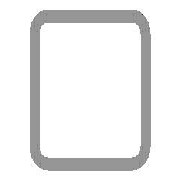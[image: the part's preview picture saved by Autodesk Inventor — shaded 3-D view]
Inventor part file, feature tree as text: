
AUTODESK INVENTOR PART (.ipt)
format: ipt  version: 2022 (Build 260153000, 153)  size: 545,792 bytes
history: native  units: mm (DEFAULTED — no unit token found)
features: other x11, surface_op x4, sketch x2, sweep x1, plane x1
ambient origin geometry x8: Origin, YZ Plane, XZ Plane, XY Plane, X Axis, Y Axis, Z Axis, Center Point
bodies: Solid1 (feature_tree), Body (feature_tree), Solid5 (feature_tree), Solid6 (feature_tree)
feature tree (19):
  parser-record x1  (decoder bookkeeping rows leaked as tree rows — omitted from the tree; the rows remain in map.json)
  other  "Driven Length"
  other  "Start Plane"
  other  "End Plane"
  sweep  "Sweep Path"
  other  "Orientation Work Plane"
  sketch  "Sketch3"  dims[d7=8.0mm d9=40.0mm]
  plane  "Work Plane3"
  sketch  "Sketch4"  dims[d11=40.0mm d12=4.0mm d13=-0.0mm d14=2479.411255mm d15=20.0mm d16=20.0mm d17=90.0deg d18=2479.411255mm d19=0.0mm d20=0.0mm d75=5.0mm d76=5.0mm d77=5.0mm d78=5.0mm d79=5.0mm d80=5.0mm d81=5.0mm d82=5.0mm d83=0.0mm d84=5.0mm d85=5.0mm d86=5.0mm d87=5.0mm d88=5.0mm d89=5.0mm d90=5.0mm d91=5.0mm d92=0.0mm d93=5.0mm d94=5.0mm d95=5.0mm d96=5.0mm d97=5.0mm d98=5.0mm d99=5.0mm d100=5.0mm d101=0.0mm d102=5.0mm d103=5.0mm d104=5.0mm d105=5.0mm d106=5.0mm d107=5.0mm d108=5.0mm d109=5.0mm d110=0.0mm]
  other  "Srf11"
  other  "Srf12"
  other  "Srf14"
  other  "Srf15"
  other  "Srf10"
  surface_op  "Boundary Patch7"
  surface_op  "Boundary Patch8"
  other  "Srf13"
  surface_op  "Boundary Patch9"
  surface_op  "Boundary Patch10"
